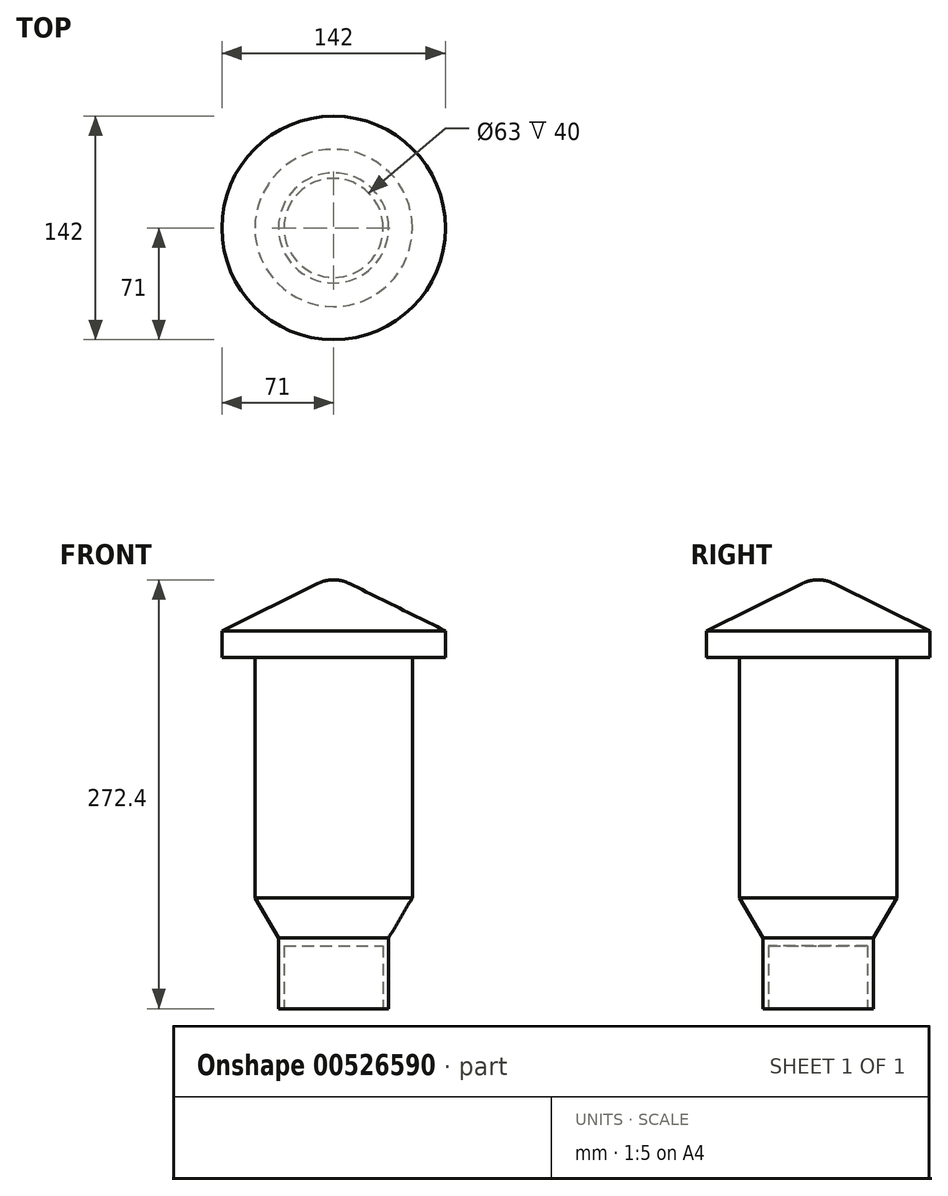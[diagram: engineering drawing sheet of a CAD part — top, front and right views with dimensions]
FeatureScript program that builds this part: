
annotation { "Feature Type Name" : "Feature", "Feature Type Description" : "" }
export const myFeature = defineFeature(function(context is Context, id is Id, definition is map)
    precondition{}
    {
        {
            var Q0;
            Q0=qCreatedBy(makeId("Front.planeOp"),FACE);
            var sketch = newSketch(context, id + "F0", { "sketchPlane" : qUnion([Q0])});
            skLineSegment(sketch, "E0", {"start": v(0, -78.66) * mm, "end": v(0, 272.4) * mm, "construction": true});
            skLineSegment(sketch, "E1", {"start": v(0, 0) * mm, "end": v(-35, 0) * mm});
            skLineSegment(sketch, "E2", {"start": v(-71, 240) * mm, "end": v(-10.1, 270.03) * mm});
            skLineSegment(sketch, "E3", {"start": v(-50, 70.39) * mm, "end": v(-35, 45) * mm});
            skLineSegment(sketch, "E4", {"start": v(-35, 45) * mm, "end": v(-35, 0) * mm});
            skLineSegment(sketch, "E5", {"start": v(-71, 223.14) * mm, "end": v(-50, 223.14) * mm});
            skLineSegment(sketch, "E6", {"start": v(-50, 223.14) * mm, "end": v(-50, 70.39) * mm});
            skLineSegment(sketch, "E7.trimOffspring", {"start": v(-71, 223.14) * mm, "end": v(-71, 240) * mm});
            skLineSegment(sketch, "E8", {"start": v(0, 275) * mm, "end": v(0, 0) * mm});
            skPoint(sketch, "E9.newPointA", {"position": v(-15, 268.5) * mm});
            skPoint(sketch, "E9.newPointB", {"position": v(0, 275) * mm});
            skLineSegment(sketch, "E9.filletArc", {"start": v(0, 275) * mm, "end": v(0, 275) * mm});
            skLineSegment(sketch, "E10", {"start": v(0.08, 272.4) * mm, "end": v(0, 272.4) * mm});
            skPoint(sketch, "E11.newPointA", {"position": v(-8, 272.4) * mm});
            skArc(sketch, "E11.filletArc", {"start": v(0.08, 272.4) * mm, "mid": v(-5.14, 271.8) * mm, "end": v(-10.1, 270.03) * mm});
            skSolve(sketch);
        }
        {
            var Q0;
            Q0=makeQuery(id+"F0.imprint","IMPRINT",FACE,{"disambiguationData":[TD([[makeQuery(id+"F0.imprint","IMPRINT",EDGE,{"derivedFrom":sQuery(id+"F0.wireOp",EDGE,"E1")}),-1.0]])]});
            var Q1;
            Q1=sQuery(id+"F0.wireOp",EDGE,"E8");
            revolve(context, id + "F1", {"entities" : qUnion([Q0]), "axis" : qUnion([Q1]), "revolveType" : RevolveType.FULL});
        }
        {
            var Q0;
            Q0=makeQuery(id+"F1.opRevolve","SWEPT_FACE",FACE,{"disambiguationData":[OSD([sQuery(id+"F0.wireOp",EDGE,"E1")])]});
            var sketch = newSketch(context, id + "F2", { "sketchPlane" : qUnion([Q0])});
            skCircle(sketch, "E12", {"center": v(0, 0) * mm, "radius": 31.5 * mm});
            skSolve(sketch);
        }
        {
            var Q0;
            Q0=makeQuery(id+"F2.imprint","IMPRINT",FACE,{"disambiguationData":[TD([[makeQuery(id+"F2.imprint","IMPRINT",EDGE,{"derivedFrom":sQuery(id+"F2.wireOp",EDGE,"E12")}),1.0]])]});
            extrude(context, id + "F3", {"entities" : qUnion([Q0]), "operationType" : NewBodyOperationType.REMOVE, "oppositeDirection" : true, "depth" : 40 * mm, "offsetDistance" : 25 * mm});
        }
    });
